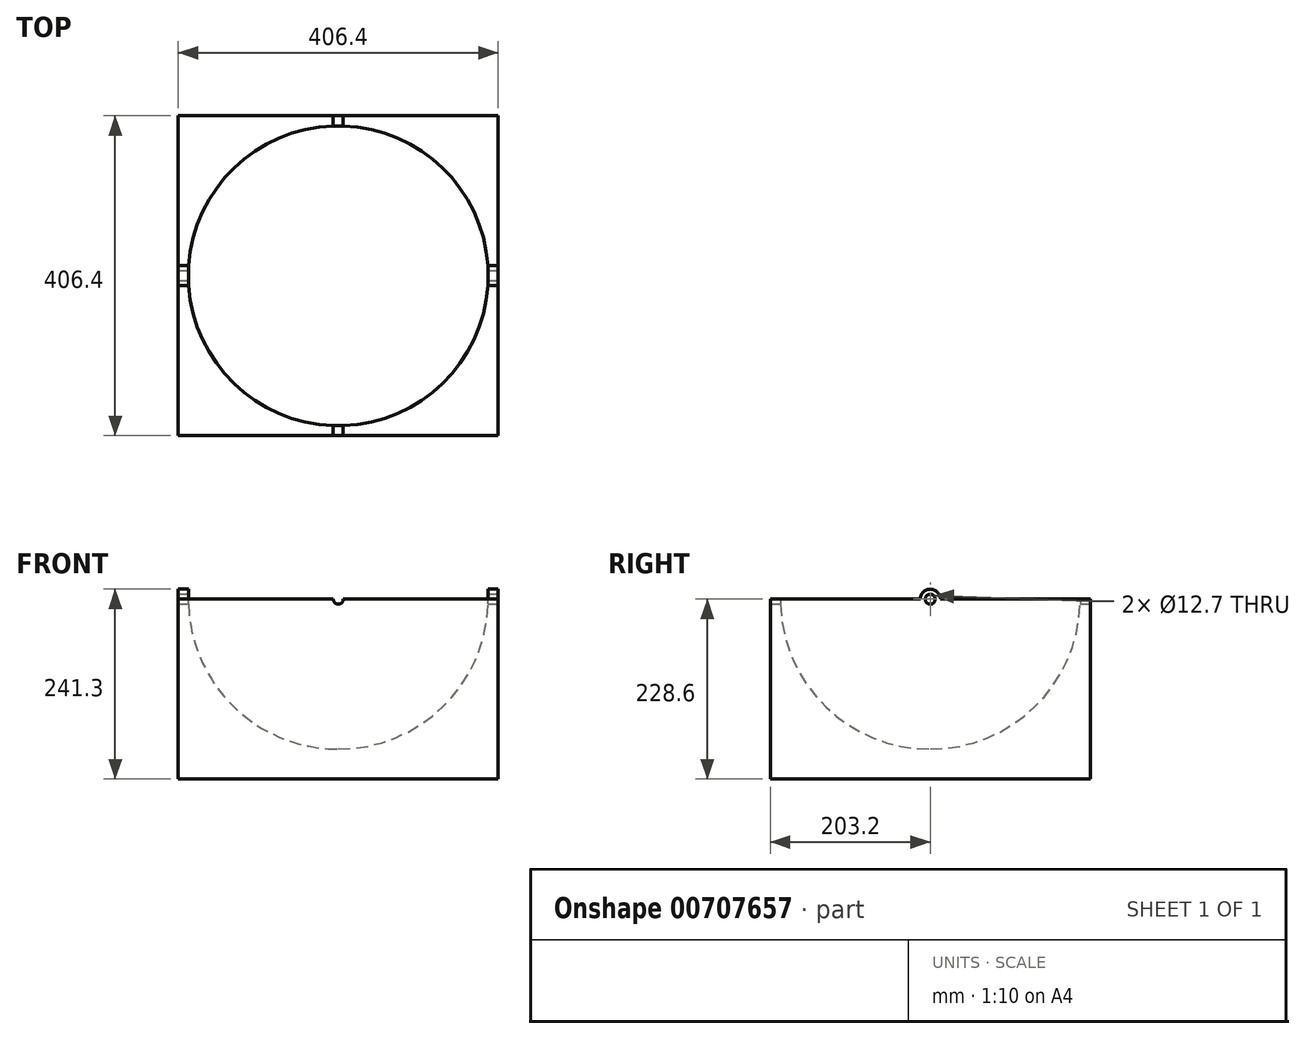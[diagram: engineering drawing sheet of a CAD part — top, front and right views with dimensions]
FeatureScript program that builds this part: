
annotation { "Feature Type Name" : "Feature", "Feature Type Description" : "" }
export const myFeature = defineFeature(function(context is Context, id is Id, definition is map)
    precondition{}
    {
        {
            var Q0;
            Q0=qCreatedBy(makeId("Front.planeOp"),FACE);
            var sketch = newSketch(context, id + "F0", { "sketchPlane" : qUnion([Q0])});
            skLineSegment(sketch, "E0.bottom", {"start": v(-203.2, 0) * mm, "end": v(203.2, 0) * mm});
            skLineSegment(sketch, "E0.top", {"start": v(-203.2, -228.6) * mm, "end": v(203.2, -228.6) * mm});
            skLineSegment(sketch, "E0.left", {"start": v(-203.2, 0) * mm, "end": v(-203.2, -228.6) * mm});
            skLineSegment(sketch, "E0.right", {"start": v(203.2, 0) * mm, "end": v(203.2, -228.6) * mm});
            skCircle(sketch, "E1", {"center": v(0, 0) * mm, "radius": 12.7 * mm});
            skCircle(sketch, "E2", {"center": v(0, 0) * mm, "radius": 6.35 * mm});
            skSolve(sketch);
        }
        {
            var Q0;
            Q0=makeQuery(id+"F0.imprint","IMPRINT",FACE,{"disambiguationData":[TD([[makeQuery(id+"F0.imprint","IMPRINT",EDGE,{"derivedFrom":sQuery(id+"F0.wireOp",EDGE,"E0.bottom")}),-1.0]])]});
            var Q1;
            Q1 = qSketchRegion(id + "F2", true);
            var Q2;
            Q2=makeQuery(id+"F0.imprint","IMPRINT",FACE,{"disambiguationData":[TD([[makeQuery(id+"F0.imprint","IMPRINT",EDGE,{"derivedFrom":sQuery(id+"F0.wireOp",EDGE,"E0.top")}),1.0]])]});
            var Q3;
            {var subQ0=sQuery(id+"F0.wireOp",EDGE,"E1");var subQ1=sQuery(id+"F0.wireOp",EDGE,"E0.bottom");var subQ2=makeQuery(id+"F0.imprint","INTERSECT",VERTEX,{"disambiguationData":[OD(0.0)],"derivedFrom":[subQ1,subQ0]});Q3=makeQuery(id+"F0.imprint","IMPRINT",FACE,{"disambiguationData":[TD([[makeQuery(id+"F0.imprint","IMPRINT",EDGE,{"disambiguationData":[TD([[subQ2,-1.0]])],"derivedFrom":subQ1}),1.0]])]});}
            extrude(context, id + "F1", {"entities" : qUnion([Q0, Q1, Q2, Q3]), "depth" : 203.2 * mm, "offsetDistance" : 25.4 * mm, "hasSecondDirection" : true, "secondDirectionOppositeDirection" : true, "secondDirectionDepth" : 203.2 * mm});
        }
        {
            var Q0;
            Q0=qCreatedBy(makeId("Front.planeOp"),FACE);
            var sketch = newSketch(context, id + "F2", { "sketchPlane" : qUnion([Q0])});
            skArc(sketch, "E3", {"start": v(0, -190.5) * mm, "mid": v(190.5, 0) * mm, "end": v(0, 190.5) * mm});
            skLineSegment(sketch, "E4", {"start": v(0, 190.5) * mm, "end": v(0, -190.5) * mm});
            skSolve(sketch);
        }
        {
            var Q0;
            Q0=makeQuery(id+"F1.opExtrude","SWEPT_FACE",FACE,{"disambiguationData":[OSD([sQuery(id+"F0.wireOp",EDGE,"E0.right")])]});
            var sketch = newSketch(context, id + "F3", { "sketchPlane" : qUnion([Q0])});
            skCircle(sketch, "E5", {"center": v(0, 0) * mm, "radius": 12.7 * mm});
            skSolve(sketch);
        }
        {
            var Q0;
            {var subQ0=sQuery(id+"F3.wireOp",EDGE,"E5");var subQ1=makeQuery(id+"F1.opExtrude","SWEPT_EDGE",EDGE,{"disambiguationData":[OSD([sQuery(id+"F0.wireOp",EDGE,"E0.bottom"),sQuery(id+"F0.wireOp",EDGE,"E0.right")])]});var subQ2=makeQuery(id+"F3.imprint","INTERSECT",VERTEX,{"disambiguationData":[OD(0.0)],"derivedFrom":[subQ1,subQ0]});Q0=makeQuery(id+"F3.imprint","IMPRINT",FACE,{"disambiguationData":[TD([[makeQuery(id+"F3.imprint","IMPRINT",EDGE,{"disambiguationData":[TD([[subQ2,-1.0]])],"derivedFrom":subQ0}),1.0]])]});}
            var Q1;
            {var subQ0=sQuery(id+"F3.wireOp",EDGE,"E5");var subQ1=makeQuery(id+"F1.opExtrude","SWEPT_EDGE",EDGE,{"disambiguationData":[OSD([sQuery(id+"F0.wireOp",EDGE,"E0.bottom"),sQuery(id+"F0.wireOp",EDGE,"E0.right")])]});var subQ2=makeQuery(id+"F3.imprint","INTERSECT",VERTEX,{"disambiguationData":[OD(0.0)],"derivedFrom":[subQ1,subQ0]});Q1=makeQuery(id+"F3.imprint","IMPRINT",FACE,{"disambiguationData":[TD([[makeQuery(id+"F3.imprint","IMPRINT",EDGE,{"disambiguationData":[TD([[subQ2,1.0]])],"derivedFrom":subQ0}),1.0]])]});}
            extrude(context, id + "F4", {"entities" : qUnion([Q0, Q1]), "operationType" : NewBodyOperationType.ADD, "oppositeDirection" : true, "depth" : 406.4 * mm, "offsetDistance" : 25.4 * mm});
        }
        {
            var Q0;
            Q0=makeQuery(id+"F4.boolean.opBoolean","MERGE",FACE,{"derivedFrom":[makeQuery(id+"F1.opExtrude","SWEPT_FACE",FACE,{"disambiguationData":[OSD([sQuery(id+"F0.wireOp",EDGE,"E0.right")])]}),makeQuery(id+"F4.opExtrude","CAP_FACE",FACE,{"disambiguationData":[OSD([sQuery(id+"F3.wireOp",EDGE,"E5")])],"isStart":true})]});
            var sketch = newSketch(context, id + "F5", { "sketchPlane" : qUnion([Q0])});
            skCircle(sketch, "E6", {"center": v(0, 0) * mm, "radius": 6.35 * mm});
            skSolve(sketch);
        }
        {
            var Q0;
            Q0=makeQuery(id+"F5.imprint","IMPRINT",FACE,{"disambiguationData":[TD([[makeQuery(id+"F5.imprint","IMPRINT",EDGE,{"derivedFrom":sQuery(id+"F5.wireOp",EDGE,"E6")}),1.0]])]});
            extrude(context, id + "F6", {"entities" : qUnion([Q0]), "operationType" : NewBodyOperationType.REMOVE, "oppositeDirection" : true, "depth" : 406.4 * mm, "offsetDistance" : 25.4 * mm});
        }
        {
            var Q0;
            Q0=makeQuery(id+"F2.imprint","IMPRINT",FACE,{"disambiguationData":[TD([[makeQuery(id+"F2.imprint","IMPRINT",EDGE,{"derivedFrom":sQuery(id+"F2.wireOp",EDGE,"E3")}),1.0]])]});
            var Q1;
            Q1=sQuery(id+"F2.wireOp",EDGE,"E4");
            revolve(context, id + "F7", {"operationType" : NewBodyOperationType.REMOVE, "surfaceOperationType" : NewSurfaceOperationType.NEW, "entities" : qUnion([Q0]), "axis" : qUnion([Q1]), "revolveType" : RevolveType.FULL, "oppositeDirection" : true});
        }
    });
